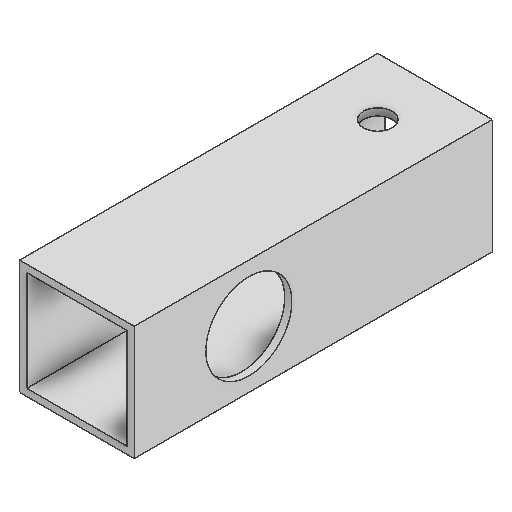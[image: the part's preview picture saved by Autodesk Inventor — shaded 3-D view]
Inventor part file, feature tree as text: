
AUTODESK INVENTOR PART (.ipt)
format: ipt  version: 2025.2 (Build 292293000, 293)  size: 137,216 bytes
history: native  units: in
note: dims shown in document units (in); Inventor stores cm internally (conversion verified against a paired STEP export)
features: extrude x3, sketch x3
ambient origin geometry x8: Origin, YZ Plane, XZ Plane, XY Plane, X Axis, Y Axis, Z Axis, Center Point
bodies: Solid1 (feature_tree)
feature tree (6):
  extrude  "Extrusion1"  Depth=1.0in
  extrude  "Extrusion2"  Depth=0.0625in
  extrude  "Extrusion3"  Depth=0.0625in
  sketch  "Sketch1"  dims[d0=1.0in d1=1.0in]
  sketch  "Sketch2"  dims[d2=0.0625in d3=0.0625in]
  sketch  "Sketch3"  dims[d4=0.0625in d5=0.0625in d6=3.125in d7=0.0in d8=0.75in d9=0.0in d10=0.0in d11=0.5in d12=1.0in d13=0.8in d14=0.25in d15=0.25in d16=0.8in d17=0.25in d18=0.5in d19=0.5in d20=0.0in d21=0.0in]
